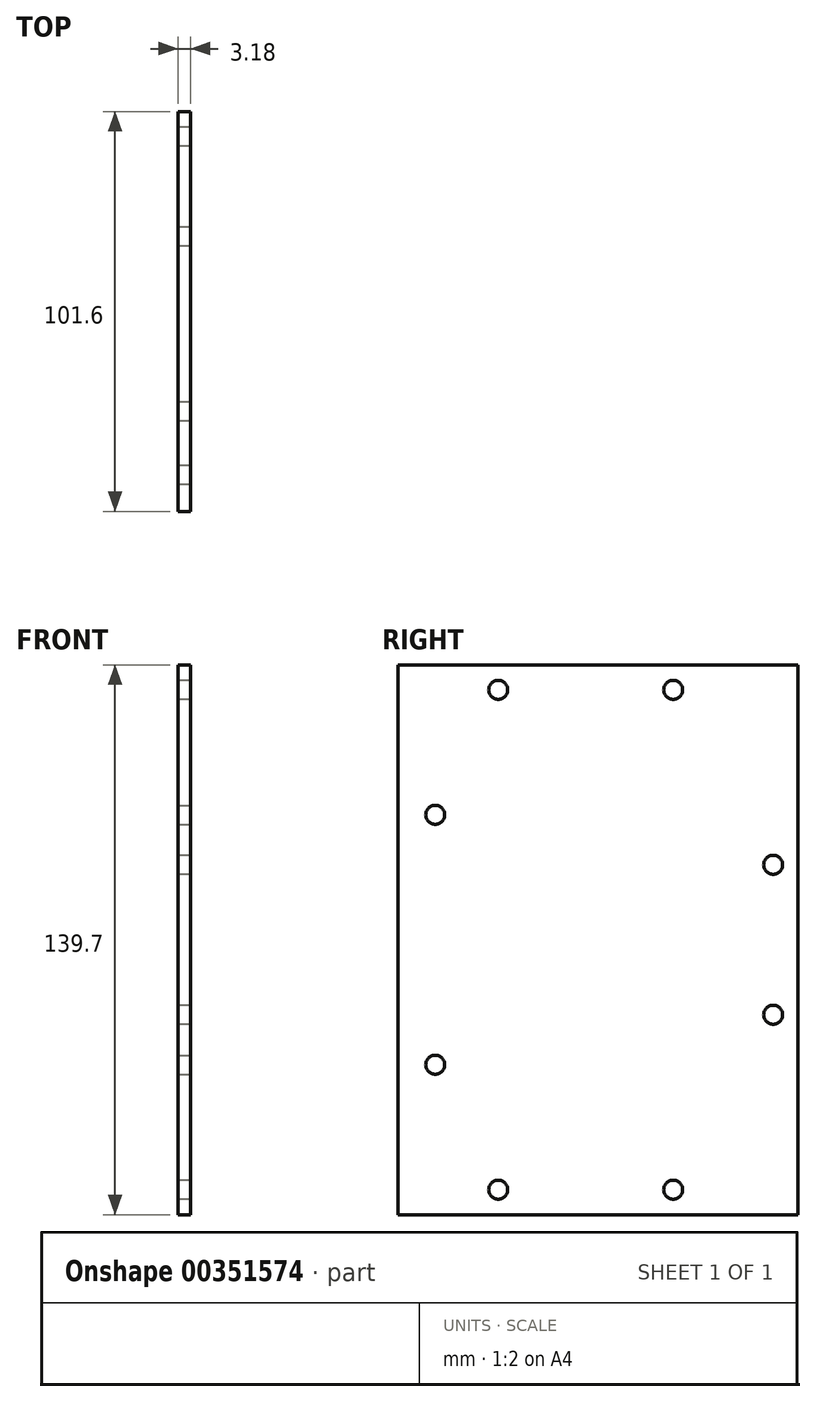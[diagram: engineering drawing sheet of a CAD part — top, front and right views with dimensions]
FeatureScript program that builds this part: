
annotation { "Feature Type Name" : "Feature", "Feature Type Description" : "" }
export const myFeature = defineFeature(function(context is Context, id is Id, definition is map)
    precondition{}
    {
        {
            var Q0;
            Q0=qCreatedBy(makeId("Top.planeOp"),FACE);
            var sketch = newSketch(context, id + "F0", { "sketchPlane" : qUnion([Q0])});
            skLineSegment(sketch, "E0.bottom", {"start": v(1.59, -50.8) * mm, "end": v(-1.59, -50.8) * mm});
            skLineSegment(sketch, "E0.top", {"start": v(1.59, 50.8) * mm, "end": v(-1.59, 50.8) * mm});
            skLineSegment(sketch, "E0.left", {"start": v(1.59, -50.8) * mm, "end": v(1.59, 50.8) * mm});
            skLineSegment(sketch, "E0.right", {"start": v(-1.59, -50.8) * mm, "end": v(-1.59, 50.8) * mm});
            skPoint(sketch, "E0.middle", {"position": v(0, 0) * mm});
            skSolve(sketch);
        }
        {
            var Q0;
            Q0 = qSketchRegion(id + "F0", true);
            extrude(context, id + "F1", {"entities" : qUnion([Q0]), "depth" : 139.7 * mm, "symmetric" : true});
        }
        {
            var Q0;
            Q0=makeQuery(id+"F1.opExtrude","SWEPT_FACE",FACE,{"disambiguationData":[OSD([sQuery(id+"F0.wireOp",EDGE,"E0.right")])]});
            var sketch = newSketch(context, id + "F2", { "sketchPlane" : qUnion([Q0])});
            skCircle(sketch, "E1", {"center": v(-44.45, -19.05) * mm, "radius": 2.41 * mm});
            skCircle(sketch, "E2.MirrorC", {"center": v(-44.45, 19.05) * mm, "radius": 2.41 * mm});
            skSolve(sketch);
        }
        {
            var Q0;
            Q0 = qSketchRegion(id + "F2", true);
            var Q1;
            Q1=makeQuery(id+"F1.opExtrude","SWEPT_FACE",FACE,{"disambiguationData":[OSD([sQuery(id+"F0.wireOp",EDGE,"E0.left")])]});
            extrude(context, id + "F3", {"entities" : qUnion([Q0]), "operationType" : NewBodyOperationType.REMOVE, "endBound" : BoundingType.UP_TO_SURFACE, "oppositeDirection" : true, "endBoundEntityFace" : qUnion([Q1]), "depth" : 25.4 * mm});
        }
        {
            var Q0;
            Q0=makeQuery(id+"F1.opExtrude","SWEPT_FACE",FACE,{"disambiguationData":[OSD([sQuery(id+"F0.wireOp",EDGE,"E0.right")])]});
            var sketch = newSketch(context, id + "F4", { "sketchPlane" : qUnion([Q0])});
            skCircle(sketch, "E3", {"center": v(-19.05, -63.5) * mm, "radius": 2.41 * mm});
            skCircle(sketch, "E4.MirrorC", {"center": v(-19.05, 63.5) * mm, "radius": 2.41 * mm});
            skSolve(sketch);
        }
        {
            var Q0;
            Q0 = qSketchRegion(id + "F4", true);
            var Q1;
            Q1=makeQuery(id+"F1.opExtrude","SWEPT_FACE",FACE,{"disambiguationData":[OSD([sQuery(id+"F0.wireOp",EDGE,"E0.left")])]});
            extrude(context, id + "F5", {"entities" : qUnion([Q0]), "operationType" : NewBodyOperationType.REMOVE, "endBound" : BoundingType.UP_TO_SURFACE, "oppositeDirection" : true, "endBoundEntityFace" : qUnion([Q1]), "depth" : 25.4 * mm});
        }
        {
            var Q0;
            Q0=makeQuery(id+"F1.opExtrude","SWEPT_FACE",FACE,{"disambiguationData":[OSD([sQuery(id+"F0.wireOp",EDGE,"E0.right")])]});
            var sketch = newSketch(context, id + "F6", { "sketchPlane" : qUnion([Q0])});
            skCircle(sketch, "E5", {"center": v(25.4, -63.5) * mm, "radius": 2.41 * mm});
            skCircle(sketch, "E6.MirrorC", {"center": v(25.4, 63.5) * mm, "radius": 2.41 * mm});
            skSolve(sketch);
        }
        {
            var Q0;
            Q0 = qSketchRegion(id + "F6", true);
            var Q1;
            Q1=makeQuery(id+"F1.opExtrude","SWEPT_FACE",FACE,{"disambiguationData":[OSD([sQuery(id+"F0.wireOp",EDGE,"E0.left")])]});
            extrude(context, id + "F7", {"entities" : qUnion([Q0]), "operationType" : NewBodyOperationType.REMOVE, "endBound" : BoundingType.UP_TO_SURFACE, "oppositeDirection" : true, "endBoundEntityFace" : qUnion([Q1]), "depth" : 25.4 * mm});
        }
        {
            var Q0;
            Q0=makeQuery(id+"F1.opExtrude","SWEPT_FACE",FACE,{"disambiguationData":[OSD([sQuery(id+"F0.wireOp",EDGE,"E0.left")])]});
            var sketch = newSketch(context, id + "F8", { "sketchPlane" : qUnion([Q0])});
            skCircle(sketch, "E7", {"center": v(-41.4, 31.75) * mm, "radius": 2.41 * mm});
            skCircle(sketch, "E8.MirrorC", {"center": v(-41.4, -31.75) * mm, "radius": 2.41 * mm});
            skSolve(sketch);
        }
        {
            var Q0;
            Q0 = qSketchRegion(id + "F8", true);
            var Q1;
            Q1=makeQuery(id+"F1.opExtrude","SWEPT_FACE",FACE,{"disambiguationData":[OSD([sQuery(id+"F0.wireOp",EDGE,"E0.right")])]});
            extrude(context, id + "F9", {"entities" : qUnion([Q0]), "operationType" : NewBodyOperationType.REMOVE, "endBound" : BoundingType.UP_TO_SURFACE, "oppositeDirection" : true, "endBoundEntityFace" : qUnion([Q1]), "depth" : 25.4 * mm});
        }
    });
